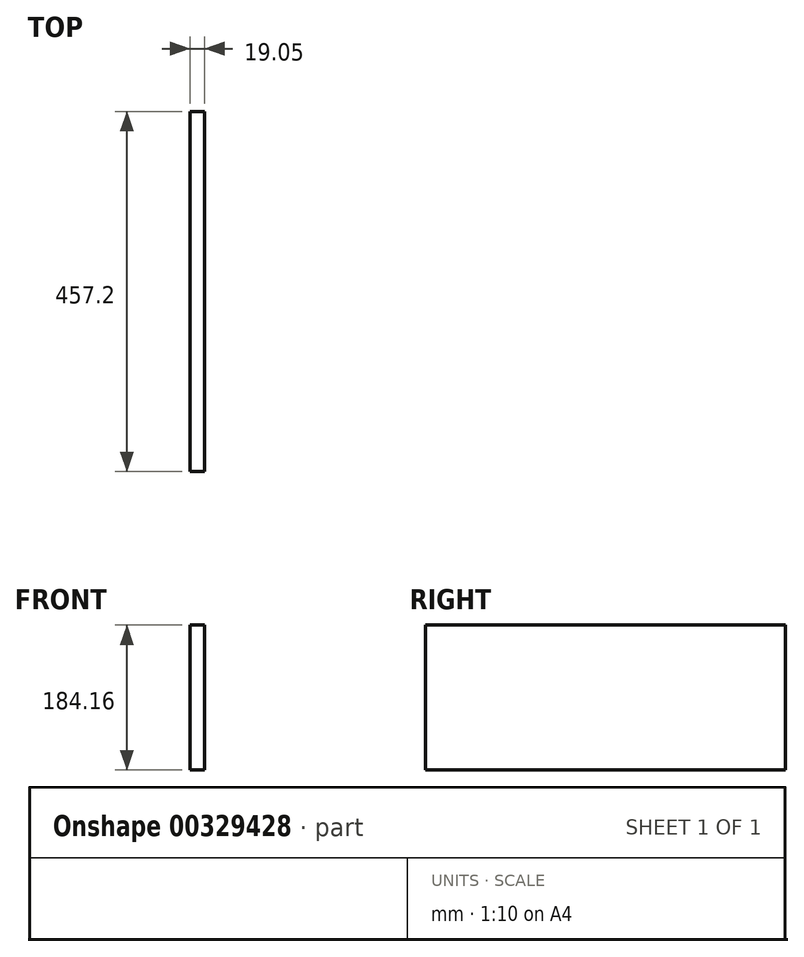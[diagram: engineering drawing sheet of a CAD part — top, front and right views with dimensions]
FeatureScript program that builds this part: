
annotation { "Feature Type Name" : "Feature", "Feature Type Description" : "" }
export const myFeature = defineFeature(function(context is Context, id is Id, definition is map)
    precondition{}
    {
        {
            var Q0;
            Q0=qCreatedBy(makeId("Right.planeOp"),FACE);
            var sketch = newSketch(context, id + "F0", { "sketchPlane" : qUnion([Q0])});
            skLineSegment(sketch, "E0.bottom", {"start": v(-228.6, 92.08) * mm, "end": v(228.6, 92.08) * mm});
            skLineSegment(sketch, "E0.top", {"start": v(-228.6, -92.08) * mm, "end": v(228.6, -92.08) * mm});
            skLineSegment(sketch, "E0.left", {"start": v(-228.6, 92.08) * mm, "end": v(-228.6, -92.08) * mm});
            skLineSegment(sketch, "E0.right", {"start": v(228.6, 92.08) * mm, "end": v(228.6, -92.08) * mm});
            skPoint(sketch, "E0.middle", {"position": v(0, 0) * mm});
            skSolve(sketch);
        }
        {
            var Q0;
            Q0 = qSketchRegion(id + "F0", true);
            extrude(context, id + "F1", {"entities" : qUnion([Q0]), "depth" : 19.05 * mm});
        }
    });
